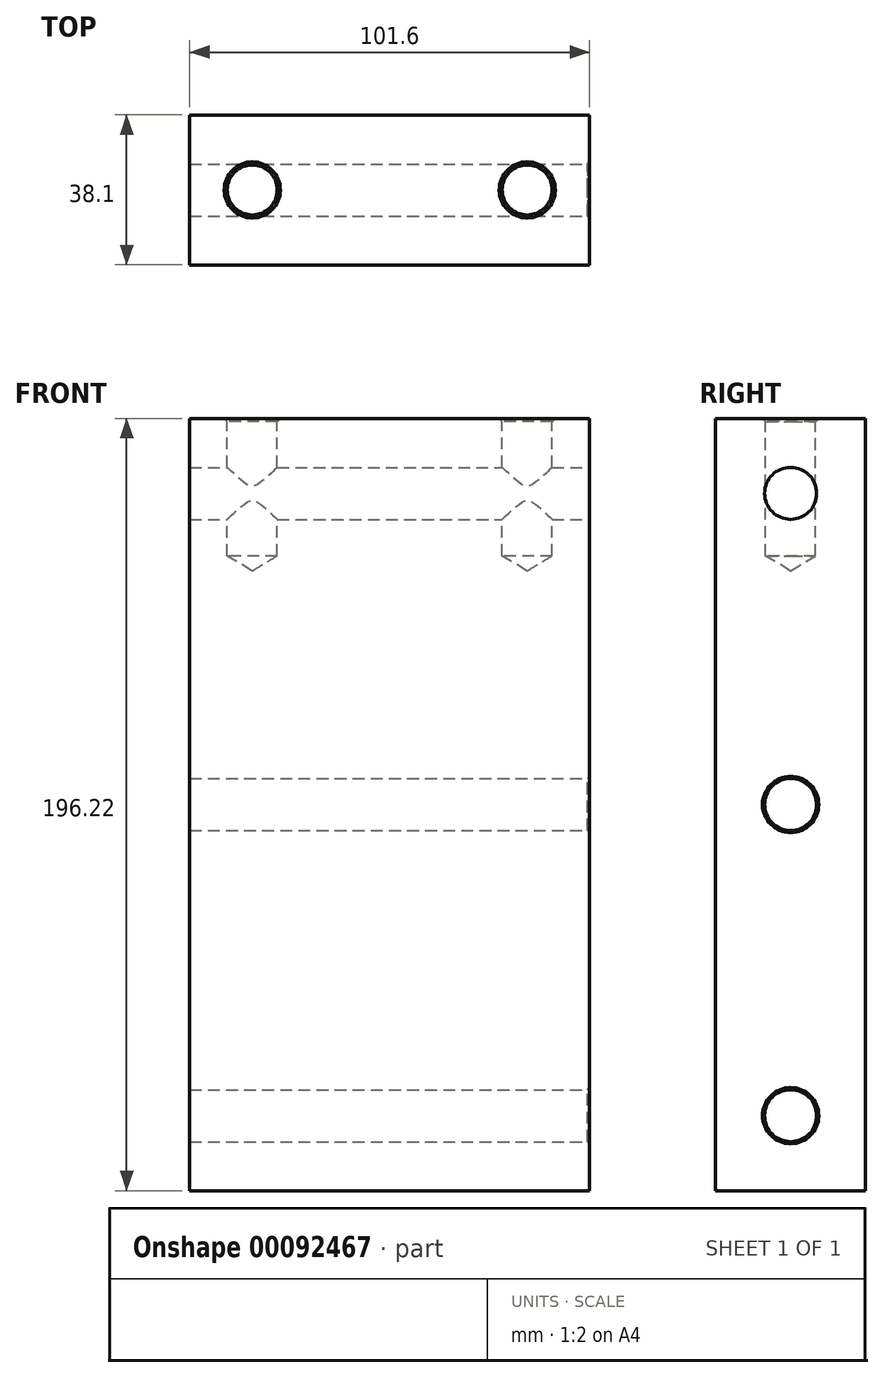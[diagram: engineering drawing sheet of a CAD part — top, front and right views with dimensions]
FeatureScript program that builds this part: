
annotation { "Feature Type Name" : "Feature", "Feature Type Description" : "" }
export const myFeature = defineFeature(function(context is Context, id is Id, definition is map)
    precondition{}
    {
        {
            var Q0;
            Q0=qCreatedBy(makeId("Top.planeOp"),FACE);
            var sketch = newSketch(context, id + "F0", { "sketchPlane" : qUnion([Q0])});
            skLineSegment(sketch, "E0", {"start": v(751.52, -407.52) * mm, "end": v(947.73, -407.52) * mm});
            skLineSegment(sketch, "E1", {"start": v(751.52, -407.52) * mm, "end": v(751.52, -445.62) * mm});
            skCircle(sketch, "E2", {"center": v(770.57, -426.57) * mm, "radius": 10.16 * mm});
            skCircle(sketch, "E3", {"center": v(928.68, -426.57) * mm, "radius": 10.16 * mm});
            skCircle(sketch, "E4", {"center": v(849.63, -426.57) * mm, "radius": 10.16 * mm});
            skCircle(sketch, "E5", {"center": v(770.57, -426.57) * mm, "radius": 6.6 * mm});
            skCircle(sketch, "E6", {"center": v(849.63, -426.57) * mm, "radius": 6.6 * mm});
            skCircle(sketch, "E7", {"center": v(928.68, -426.57) * mm, "radius": 6.6 * mm});
            skLineSegment(sketch, "E8", {"start": v(947.73, -407.52) * mm, "end": v(947.73, -445.62) * mm});
            skLineSegment(sketch, "E9", {"start": v(947.73, -445.62) * mm, "end": v(751.52, -445.62) * mm});
            skLineSegment(sketch, "E10", {"start": v(700.72, -407.52) * mm, "end": v(700.72, -445.62) * mm});
            skLineSegment(sketch, "E11", {"start": v(599.12, -445.62) * mm, "end": v(599.12, -407.52) * mm});
            skLineSegment(sketch, "E12", {"start": v(700.72, -407.52) * mm, "end": v(599.12, -407.52) * mm});
            skLineSegment(sketch, "E13", {"start": v(700.72, -445.62) * mm, "end": v(599.12, -445.62) * mm});
            skCircle(sketch, "E14", {"center": v(615, -426.57) * mm, "radius": 6.35 * mm});
            skCircle(sketch, "E15", {"center": v(684.84, -426.57) * mm, "radius": 6.35 * mm});
            skSolve(sketch);
        }
        {
            var Q0;
            Q0=makeQuery(id+"F0.imprint","IMPRINT",FACE,{"disambiguationData":[TD([[makeQuery(id+"F0.imprint","IMPRINT",EDGE,{"derivedFrom":sQuery(id+"F0.wireOp",EDGE,"E5")}),-1.0]])]});
            var Q1;
            Q1=makeQuery(id+"F0.imprint","IMPRINT",FACE,{"disambiguationData":[TD([[makeQuery(id+"F0.imprint","IMPRINT",EDGE,{"derivedFrom":sQuery(id+"F0.wireOp",EDGE,"E6")}),-1.0]])]});
            var Q2;
            Q2=makeQuery(id+"F0.imprint","IMPRINT",FACE,{"disambiguationData":[TD([[makeQuery(id+"F0.imprint","IMPRINT",EDGE,{"derivedFrom":sQuery(id+"F0.wireOp",EDGE,"E7")}),-1.0]])]});
            var Q3;
            Q3=makeQuery(id+"F0.imprint","IMPRINT",FACE,{"disambiguationData":[TD([[makeQuery(id+"F0.imprint","IMPRINT",EDGE,{"derivedFrom":sQuery(id+"F0.wireOp",EDGE,"E2")}),-1.0]])]});
            var Q4;
            Q4=makeQuery(id+"F0.imprint","IMPRINT",FACE,{"disambiguationData":[TD([[makeQuery(id+"F0.imprint","IMPRINT",EDGE,{"derivedFrom":sQuery(id+"F0.wireOp",EDGE,"E3")}),-1.0]])]});
            var Q5;
            Q5=makeQuery(id+"F0.imprint","IMPRINT",FACE,{"disambiguationData":[TD([[makeQuery(id+"F0.imprint","IMPRINT",EDGE,{"derivedFrom":sQuery(id+"F0.wireOp",EDGE,"E4")}),-1.0]])]});
            var Q6;
            Q6=makeQuery(id+"F0.imprint","IMPRINT",FACE,{"disambiguationData":[TD([[makeQuery(id+"F0.imprint","IMPRINT",EDGE,{"derivedFrom":sQuery(id+"F0.wireOp",EDGE,"E0")}),-1.0]])]});
            extrude(context, id + "F1", {"entities" : qUnion([Q0, Q1, Q2, Q3, Q4, Q5, Q6]), "oppositeDirection" : true, "depth" : 101.6 * mm});
        }
        {
            var Q0;
            Q0=sQuery(id+"F0.wireOp",VERTEX,"E3.center");
            var Q1;
            Q1=sQuery(id+"F0.wireOp",VERTEX,"E4.center");
            var Q2;
            Q2=makeQuery(id+"F1.opExtrude","SWEPT_BODY",BODY,{"disambiguationData":[OSD([sQuery(id+"F0.wireOp",EDGE,"E0"),sQuery(id+"F0.wireOp",EDGE,"E1"),sQuery(id+"F0.wireOp",EDGE,"E8"),sQuery(id+"F0.wireOp",EDGE,"E9")])]});
            hole(context, id + "F2", {"style" : HoleStyle.C_SINK, "endStyle" : HoleEndStyle.BLIND, "holeDiameter" : 12.7 * mm, "cSinkDiameter" : 14.29 * mm, "cSinkAngle" : 90 * degree, "holeDepth" : 34.92 * mm, "startFromSketch" : true, "locations" : qUnion([Q0, Q1]), "scope" : qUnion([Q2])});
        }
        {
            var Q0;
            Q0=makeQuery(id+"F1.opExtrude","SWEPT_BODY",BODY,{"disambiguationData":[OSD([sQuery(id+"F0.wireOp",EDGE,"E0"),sQuery(id+"F0.wireOp",EDGE,"E1"),sQuery(id+"F0.wireOp",EDGE,"E8"),sQuery(id+"F0.wireOp",EDGE,"E9")])]});
            var Q1;
            Q1=sQuery(id+"F0.wireOp",EDGE,"E1");
            transform(context, id + "F3", {"entities" : qUnion([Q0]), "transformType" : TransformType.ROTATION, "transformAxis" : qUnion([Q1]), "angle" : 90 * degree, "oppositeDirection" : true, "makeCopy" : false});
        }
        {
            var Q0;
            Q0=makeQuery(id+"F1.opExtrude","SWEPT_BODY",BODY,{"disambiguationData":[OSD([sQuery(id+"F0.wireOp",EDGE,"E0"),sQuery(id+"F0.wireOp",EDGE,"E1"),sQuery(id+"F0.wireOp",EDGE,"E8"),sQuery(id+"F0.wireOp",EDGE,"E9")])]});
            var Q1;
            Q1=sQuery(id+"F0.wireOp",VERTEX,"E1.start");
            var Q2;
            Q2=sQuery(id+"F0.wireOp",VERTEX,"E12.start");
            transform(context, id + "F4", {"entities" : qUnion([Q0]), "transformType" : TransformType.TRANSLATION_ENTITY, "oppositeDirectionEntity" : false, "transformLine" : qUnion([Q1, Q2]), "makeCopy" : false});
        }
        {
            var Q0;
            Q0=sQuery(id+"F0.wireOp",VERTEX,"E14.center");
            var Q1;
            Q1=sQuery(id+"F0.wireOp",VERTEX,"E15.center");
            var Q2;
            Q2=makeQuery(id+"F1.opExtrude","SWEPT_BODY",BODY,{"disambiguationData":[OSD([sQuery(id+"F0.wireOp",EDGE,"E0"),sQuery(id+"F0.wireOp",EDGE,"E1"),sQuery(id+"F0.wireOp",EDGE,"E8"),sQuery(id+"F0.wireOp",EDGE,"E9")])]});
            hole(context, id + "F5", {"style" : HoleStyle.C_SINK, "endStyle" : HoleEndStyle.BLIND, "holeDiameter" : 12.7 * mm, "cSinkDiameter" : 14.29 * mm, "cSinkAngle" : 90 * degree, "holeDepth" : 34.92 * mm, "startFromSketch" : true, "locations" : qUnion([Q0, Q1]), "scope" : qUnion([Q2])});
        }
    });
